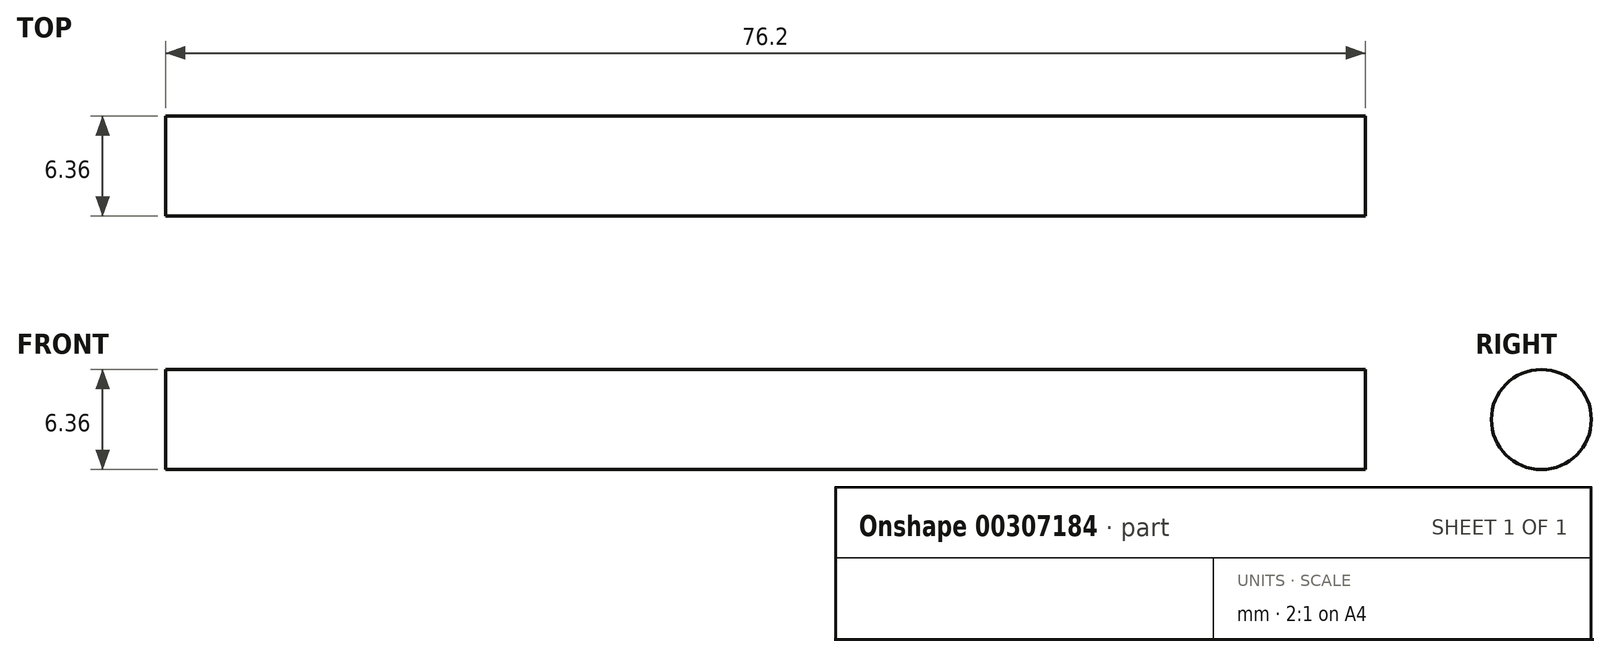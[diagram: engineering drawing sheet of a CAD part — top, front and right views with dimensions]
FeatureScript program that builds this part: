
annotation { "Feature Type Name" : "Feature", "Feature Type Description" : "" }
export const myFeature = defineFeature(function(context is Context, id is Id, definition is map)
    precondition{}
    {
        {
            var Q0;
            Q0=qCreatedBy(makeId("Right.planeOp"),FACE);
            var sketch = newSketch(context, id + "F0", { "sketchPlane" : qUnion([Q0])});
            skCircle(sketch, "E0", {"center": v(0, 0) * mm, "radius": 3.18 * mm});
            skSolve(sketch);
        }
        {
            var Q0;
            Q0 = qSketchRegion(id + "F0", true);
            extrude(context, id + "F1", {"entities" : qUnion([Q0]), "depth" : 76.2 * mm});
        }
    });
